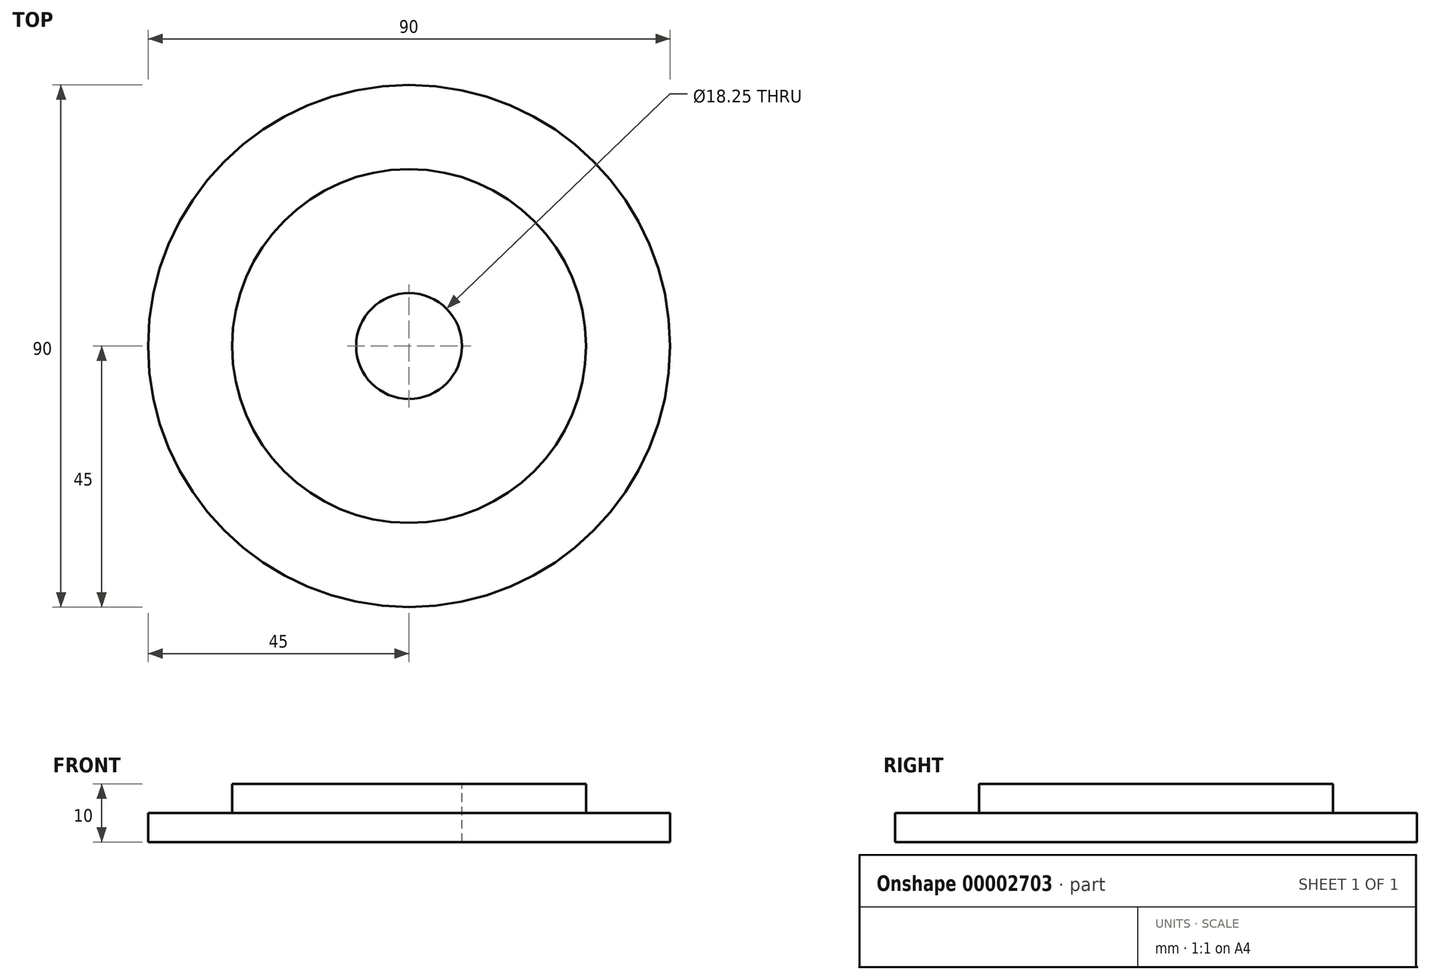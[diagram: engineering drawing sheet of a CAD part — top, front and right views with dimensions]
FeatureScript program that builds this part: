
annotation { "Feature Type Name" : "Feature", "Feature Type Description" : "" }
export const myFeature = defineFeature(function(context is Context, id is Id, definition is map)
    precondition{}
    {
        {
            var Q0;
            Q0=qCreatedBy(makeId("Top.planeOp"),FACE);
            var sketch = newSketch(context, id + "F0", { "sketchPlane" : qUnion([Q0])});
            skCircle(sketch, "E0", {"center": v(0, 0) * mm, "radius": 45 * mm});
            skSolve(sketch);
        }
        {
            var Q0;
            Q0 = qSketchRegion(id + "F0", true);
            extrude(context, id + "F1", {"entities" : qUnion([Q0]), "depth" : 5 * mm});
        }
        {
            var Q0;
            Q0=makeQuery(id+"F1.opExtrude","CAP_FACE",FACE,{"disambiguationData":[OSD([sQuery(id+"F0.wireOp",EDGE,"E0")])],"isStart":false});
            var sketch = newSketch(context, id + "F2", { "sketchPlane" : qUnion([Q0])});
            skCircle(sketch, "E1", {"center": v(0, 0) * mm, "radius": 30.5 * mm});
            skSolve(sketch);
        }
        {
            var Q0;
            Q0 = qSketchRegion(id + "F2", true);
            extrude(context, id + "F3", {"entities" : qUnion([Q0]), "operationType" : NewBodyOperationType.ADD, "depth" : 5 * mm});
        }
        {
            var Q0;
            Q0=makeQuery(id+"F3.opExtrude","CAP_FACE",FACE,{"disambiguationData":[OSD([sQuery(id+"F2.wireOp",EDGE,"E1")])],"isStart":false});
            var sketch = newSketch(context, id + "F4", { "sketchPlane" : qUnion([Q0])});
            skCircle(sketch, "E2", {"center": v(0, 0) * mm, "radius": 9.12 * mm});
            skSolve(sketch);
        }
        {
            var Q0;
            Q0 = qSketchRegion(id + "F4", true);
            extrude(context, id + "F5", {"entities" : qUnion([Q0]), "operationType" : NewBodyOperationType.REMOVE, "oppositeDirection" : true, "depth" : 25 * mm});
        }
    });
